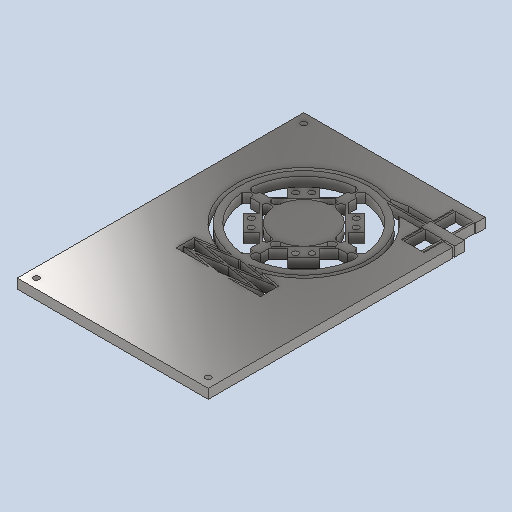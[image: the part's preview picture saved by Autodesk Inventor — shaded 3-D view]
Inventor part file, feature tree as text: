
AUTODESK INVENTOR PART (.ipt)
format: ipt  version: 2023 (Build 270158000, 158)  size: 750,592 bytes
history: native  units: mm
features: extrude x10, sketch x10
ambient origin geometry x8: Origin, YZ Plane, XZ Plane, XY Plane, X Axis, Y Axis, Z Axis, Center Point
bodies: Solid1 (feature_tree)
feature tree (20):
  extrude  "Extrusion1"  Depth=100.0mm
  extrude  "Extrusion6"  TaperAngle=0.0deg  [1 undecoded]
  extrude  "Extrusion7"  Depth=1.0mm
  extrude  "Extrusion10"  Depth=1.0mm
  extrude  "Extrusion11"  Depth=50.0mm
  extrude  "Extrusion12"  Depth=30.0mm
  extrude  "Extrusion13"  Depth=67.082039mm
  extrude  "Extrusion14"  Depth=0.5mm
  extrude  "Extrusion15"  Depth=5.0mm
  extrude  "Extrusion16"  Depth=5.0mm
  sketch  "Sketch1"  dims[d0=150.0mm d1=100.0mm]
  sketch  "Sketch6"  dims[d2=5.0mm d3=0.0mm]
  sketch  "Sketch7"  dims[d14=1.0mm d16=1.0mm]
  sketch  "Sketch9"  dims[d19=1.0mm d23=52.849025mm d24=57.849025mm]
  sketch  "Sketch11"  dims[d25=67.849025mm]
  sketch  "Sketch12"  dims[d31=45.0deg d32=45.0deg d33=45.0deg d34=45.0deg d40=45.0deg d45=45.0deg d46=45.0deg d47=45.0deg d78=50.0mm]
  sketch  "Sketch13"  dims[d79=50.0mm d80=30.0mm]
  sketch  "Sketch14"  dims[d81=60.0mm d82=67.082039mm]
  sketch  "Sketch15"  dims[d83=0.5mm d84=0.5mm]
  sketch  "Sketch16"  dims[d91=72.082039mm d92=5.0mm d93=2.5mm d94=2.5mm d95=45.0deg d96=45.0deg d97=0.5mm d98=0.5mm d99=0.5mm d100=45.0deg d101=45.0deg d102=6.0mm d103=7.0mm d104=3.0mm d105=3.0mm d106=3.0mm d107=3.0mm d108=7.5mm d109=3.0mm d110=6.0mm d111=7.0mm d112=3.0mm d113=3.0mm d114=3.0mm d115=40.0mm d117=360.0deg d119=10.0mm d120=0.0mm d125=45.0deg d128=10.0mm d133=12.0mm d134=12.0mm d135=5.0mm d136=1.0mm d137=1.0mm d138=1.0mm d139=1.0mm d140=0.5mm d141=0.5mm d142=11.0mm d144=11.0mm d145=11.0mm d146=10.0mm d147=11.0mm d154=5.0mm d155=0.0mm d164=5.0mm d167=5.0mm d168=1.0mm d169=0.0mm d170=5.0mm d171=1.0mm d172=2.0mm d179=1.0mm d180=1.0mm d182=1.013794mm d183=20.0mm d185=6.013794mm d186=10.0mm d188=10.0mm d190=1.0mm d191=1.0mm d200=5.0mm d201=0.0mm d202=5.0mm d203=0.0mm d204=1.0mm d205=1.0mm d206=1.0mm d207=1.0mm d208=5.0mm d209=5.0mm d214=3.0mm d220=67.082039mm d221=5.0mm d222=0.0mm d223=5.0mm d224=0.0mm d225=5.0mm d226=0.0mm d227=5.0mm d228=5.0mm d229=5.0mm d230=5.0mm d231=5.0mm d232=5.0mm d233=3.0mm d234=3.0mm d235=3.0mm d236=5.0mm d237=0.0mm d238=2.0mm d239=2.0mm d240=0.7mm d241=4.3mm d243=1.0mm d244=3.0mm d245=3.0mm d246=0.5mm d247=4.3mm d248=4.3mm d249=2.2mm d250=2.2mm d251=40.0mm d253=360.0deg d255=5.0mm d256=0.0mm d257=40.0mm d259=360.0deg d261=5.0mm d262=0.0mm d258=0.872665mm d260=0.872665mm]
note: 1 required parameter value undecoded (feature->parameter linkage not recoverable at this tier; creation-order binding heuristic only, values carry confidence <= 0.55)
